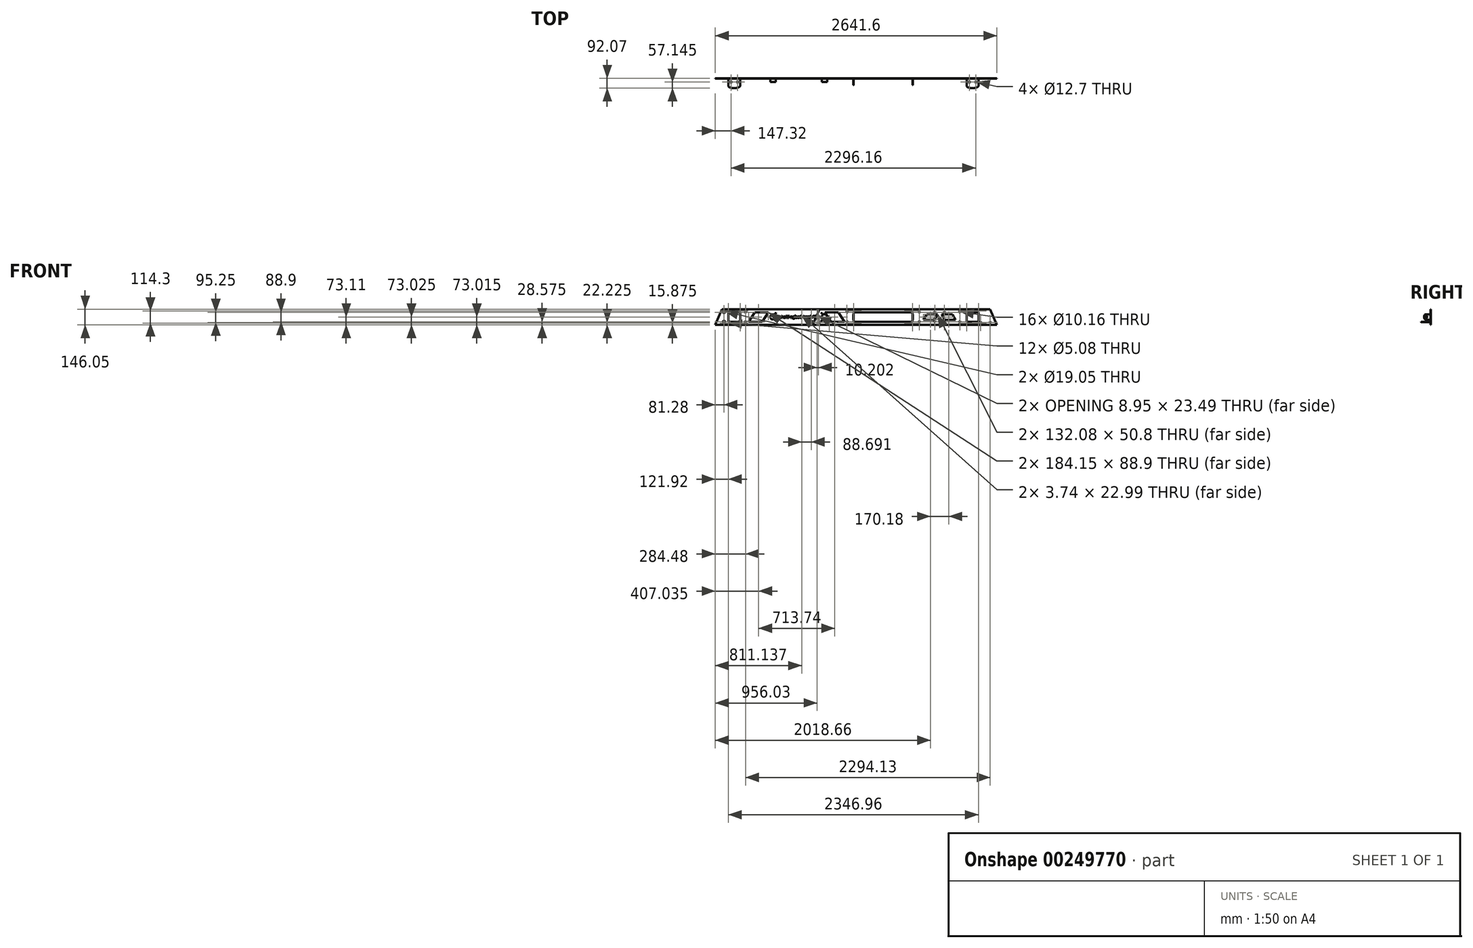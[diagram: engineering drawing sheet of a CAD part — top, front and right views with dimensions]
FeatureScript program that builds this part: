
annotation { "Feature Type Name" : "Feature", "Feature Type Description" : "" }
export const myFeature = defineFeature(function(context is Context, id is Id, definition is map)
    precondition{}
    {
        {
            var Q0;
            Q0=qCreatedBy(makeId("Front.planeOp"),FACE);
            var sketch = newSketch(context, id + "F0", { "sketchPlane" : qUnion([Q0])});
            skLineSegment(sketch, "E0", {"start": v(0, 0) * mm, "end": v(-863.6, 0) * mm});
            skLineSegment(sketch, "E1", {"start": v(-863.6, 0) * mm, "end": v(-800.1, 146.05) * mm});
            skLineSegment(sketch, "E2", {"start": v(-800.1, 146.05) * mm, "end": v(59.06, 146.05) * mm});
            skLineSegment(sketch, "E3", {"start": v(0, 0) * mm, "end": v(0, 425.14) * mm, "construction": true});
            skLineSegment(sketch, "E4.MirrorCS", {"start": v(800.1, 146.05) * mm, "end": v(-59.06, 146.05) * mm});
            skLineSegment(sketch, "E5.MirrorCS", {"start": v(863.6, 0) * mm, "end": v(800.1, 146.05) * mm});
            skLineSegment(sketch, "E6.MirrorCS", {"start": v(0, 0) * mm, "end": v(863.6, 0) * mm});
            skSolve(sketch);
        }
        {
            var Q0;
            Q0=qSketchRegion(id+"F0",true);
            extrude(context, id + "F1", {"entities" : qUnion([Q0]), "oppositeDirection" : true, "depth" : 3.17 * mm});
        }
        {
            var Q0;
            Q0=makeQuery(id+"F1.opExtrude","CAP_FACE",FACE,{"disambiguationData":[OSD([sQuery(id+"F0.wireOp",EDGE,"E0"),sQuery(id+"F0.wireOp",EDGE,"E1"),sQuery(id+"F0.wireOp",EDGE,"E2"),sQuery(id+"F0.wireOp",EDGE,"E4.MirrorCS"),sQuery(id+"F0.wireOp",EDGE,"E5.MirrorCS"),sQuery(id+"F0.wireOp",EDGE,"E6.MirrorCS")])],"isStart":true});
            var sketch = newSketch(context, id + "F2", { "sketchPlane" : qUnion([Q0])});
            skLineSegment(sketch, "E7.0", {"start": v(-863.6, 0) * mm, "end": v(-800.1, 146.05) * mm});
            skLineSegment(sketch, "E8", {"start": v(-800.1, 146.05) * mm, "end": v(-1714.5, 146.05) * mm});
            skLineSegment(sketch, "E9", {"start": v(-1714.5, 146.05) * mm, "end": v(-1778, 0) * mm});
            skLineSegment(sketch, "E10", {"start": v(-1778, 0) * mm, "end": v(-863.6, 0) * mm});
            skSolve(sketch);
        }
        {
            var Q0;
            Q0=qSketchRegion(id+"F2",true);
            var Q1;
            Q1=makeQuery(id+"F1.opExtrude","CAP_FACE",FACE,{"disambiguationData":[OSD([sQuery(id+"F0.wireOp",EDGE,"E0"),sQuery(id+"F0.wireOp",EDGE,"E1"),sQuery(id+"F0.wireOp",EDGE,"E2"),sQuery(id+"F0.wireOp",EDGE,"E4.MirrorCS"),sQuery(id+"F0.wireOp",EDGE,"E5.MirrorCS"),sQuery(id+"F0.wireOp",EDGE,"E6.MirrorCS")])],"isStart":false});
            extrude(context, id + "F3", {"entities" : qUnion([Q0]), "endBound" : BoundingType.UP_TO_SURFACE, "oppositeDirection" : true, "endBoundEntityFace" : qUnion([Q1]), "depth" : 25.4 * mm});
        }
        {
            var Q0;
            Q0=makeQuery(id+"F1.opExtrude","CAP_FACE",FACE,{"disambiguationData":[OSD([sQuery(id+"F0.wireOp",EDGE,"E0"),sQuery(id+"F0.wireOp",EDGE,"E1"),sQuery(id+"F0.wireOp",EDGE,"E2"),sQuery(id+"F0.wireOp",EDGE,"E4.MirrorCS"),sQuery(id+"F0.wireOp",EDGE,"E5.MirrorCS"),sQuery(id+"F0.wireOp",EDGE,"E6.MirrorCS")])],"isStart":false});
            var sketch = newSketch(context, id + "F4", { "sketchPlane" : qUnion([Q0])});
            skLineSegment(sketch, "E11", {"start": v(-831.85, 73.02) * mm, "end": v(1871.27, 73.02) * mm, "construction": true});
            skCircle(sketch, "E12", {"center": v(1236.69, 73.02) * mm, "radius": 25.4 * mm});
            skCircle(sketch, "E13", {"center": v(754.09, 73.02) * mm, "radius": 25.4 * mm});
            skSolve(sketch);
        }
        {
            var Q0;
            Q0=qSketchRegion(id+"F4",true);
            extrude(context, id + "F5", {"entities" : qUnion([Q0]), "operationType" : NewBodyOperationType.ADD, "depth" : 31.75 * mm});
        }
        {
            var Q0;
            Q0=makeQuery(id+"F1.opExtrude","CAP_FACE",FACE,{"disambiguationData":[OSD([sQuery(id+"F0.wireOp",EDGE,"E0"),sQuery(id+"F0.wireOp",EDGE,"E1"),sQuery(id+"F0.wireOp",EDGE,"E2"),sQuery(id+"F0.wireOp",EDGE,"E4.MirrorCS"),sQuery(id+"F0.wireOp",EDGE,"E5.MirrorCS"),sQuery(id+"F0.wireOp",EDGE,"E6.MirrorCS")])],"isStart":true});
            var sketch = newSketch(context, id + "F6", { "sketchPlane" : qUnion([Q0])});
            skLineSegment(sketch, "E14", {"start": v(800.1, 146.05) * mm, "end": v(-1714.5, 146.05) * mm, "construction": true});
            skLineSegment(sketch, "E15", {"start": v(-457.2, 146.05) * mm, "end": v(-457.2, 926.93) * mm, "construction": true});
            skPoint(sketch, "E15.endSnap0", {"position": v(-457.2, 146.05) * mm});
            skLineSegment(sketch, "E16", {"start": v(831.85, 73.02) * mm, "end": v(-1878.84, 73.02) * mm, "construction": true});
            skLineSegment(sketch, "E17.bottom", {"start": v(-478.8, 28.58) * mm, "end": v(72.39, 28.58) * mm});
            skLineSegment(sketch, "E17.top", {"start": v(-478.8, 117.48) * mm, "end": v(72.39, 117.48) * mm});
            skLineSegment(sketch, "E17.left", {"start": v(-478.8, 28.58) * mm, "end": v(-478.8, 117.48) * mm});
            skLineSegment(sketch, "E17.right", {"start": v(72.39, 28.58) * mm, "end": v(72.39, 117.48) * mm});
            skPoint(sketch, "E17.middle", {"position": v(-203.2, 73.02) * mm});
            skLineSegment(sketch, "E18.bottom", {"start": v(690.88, 28.58) * mm, "end": v(579.12, 28.58) * mm});
            skLineSegment(sketch, "E18.top", {"start": v(690.88, 117.48) * mm, "end": v(579.12, 117.47) * mm});
            skLineSegment(sketch, "E18.left", {"start": v(690.88, 28.58) * mm, "end": v(690.88, 117.48) * mm});
            skLineSegment(sketch, "E18.right", {"start": v(579.12, 28.58) * mm, "end": v(579.12, 117.47) * mm});
            skPoint(sketch, "E18.middle", {"position": v(635, 73.03) * mm});
            skCircle(sketch, "E19", {"center": v(135.89, 117.48) * mm, "radius": 5.08 * mm});
            skCircle(sketch, "E20", {"center": v(135.89, 28.58) * mm, "radius": 5.08 * mm});
            skCircle(sketch, "E21", {"center": v(515.62, 28.58) * mm, "radius": 5.08 * mm});
            skCircle(sketch, "E22", {"center": v(515.62, 117.47) * mm, "radius": 5.08 * mm});
            skCircle(sketch, "E23", {"center": v(-542.3, 117.48) * mm, "radius": 5.08 * mm});
            skCircle(sketch, "E24", {"center": v(-542.3, 28.58) * mm, "radius": 5.08 * mm});
            skCircle(sketch, "E25", {"center": v(-478.8, 130.18) * mm, "radius": 2.54 * mm});
            skCircle(sketch, "E26", {"center": v(72.39, 130.18) * mm, "radius": 2.54 * mm});
            skCircle(sketch, "E27.MirrorC", {"center": v(-478.8, 15.87) * mm, "radius": 2.54 * mm});
            skCircle(sketch, "E28.MirrorC", {"center": v(72.39, 15.87) * mm, "radius": 2.54 * mm});
            skCircle(sketch, "E29", {"center": v(579.12, 130.17) * mm, "radius": 2.54 * mm});
            skCircle(sketch, "E30", {"center": v(690.88, 130.18) * mm, "radius": 2.54 * mm});
            skCircle(sketch, "E31.MirrorC", {"center": v(579.12, 15.88) * mm, "radius": 2.54 * mm});
            skCircle(sketch, "E32.MirrorC", {"center": v(690.88, 15.88) * mm, "radius": 2.54 * mm});
            skLineSegment(sketch, "E33.bottom", {"start": v(-1544.32, 28.57) * mm, "end": v(-1656.08, 28.57) * mm});
            skLineSegment(sketch, "E33.top", {"start": v(-1544.32, 117.47) * mm, "end": v(-1656.08, 117.47) * mm});
            skLineSegment(sketch, "E33.left", {"start": v(-1544.32, 28.57) * mm, "end": v(-1544.32, 117.47) * mm});
            skLineSegment(sketch, "E33.right", {"start": v(-1656.08, 28.57) * mm, "end": v(-1656.08, 117.47) * mm});
            skPoint(sketch, "E33.middle", {"position": v(-1600.2, 73.02) * mm});
            skCircle(sketch, "E34", {"center": v(-1493.52, 117.47) * mm, "radius": 5.08 * mm});
            skCircle(sketch, "E35", {"center": v(-1493.52, 28.57) * mm, "radius": 5.08 * mm});
            skCircle(sketch, "E36", {"center": v(-1696.72, 117.47) * mm, "radius": 9.53 * mm});
            skCircle(sketch, "E37", {"center": v(-1696.72, 28.57) * mm, "radius": 9.53 * mm});
            skCircle(sketch, "E38", {"center": v(-1656.08, 130.17) * mm, "radius": 2.54 * mm});
            skCircle(sketch, "E39", {"center": v(-1544.32, 130.17) * mm, "radius": 2.54 * mm});
            skCircle(sketch, "E40.MirrorC", {"center": v(-1656.08, 15.87) * mm, "radius": 2.54 * mm});
            skCircle(sketch, "E41.MirrorC", {"center": v(-1544.32, 15.87) * mm, "radius": 2.54 * mm});
            skLineSegment(sketch, "E42", {"start": v(135.89, 117.47) * mm, "end": v(515.62, 117.48) * mm, "construction": true});
            skLineSegment(sketch, "E43", {"start": v(325.75, 117.48) * mm, "end": v(325.75, 228.13) * mm, "construction": true});
            skCircle(sketch, "E44", {"center": v(371.1, 117.48) * mm, "radius": 5.08 * mm});
            skCircle(sketch, "E45.MirrorC", {"center": v(280.42, 117.48) * mm, "radius": 5.08 * mm});
            skCircle(sketch, "E46.MirrorC", {"center": v(280.42, 28.57) * mm, "radius": 5.08 * mm});
            skCircle(sketch, "E47.MirrorC", {"center": v(371.1, 28.57) * mm, "radius": 5.08 * mm});
            skLineSegment(sketch, "E48", {"start": v(344.8, 98.42) * mm, "end": v(446.4, 98.42) * mm});
            skLineSegment(sketch, "E49", {"start": v(446.4, 98.43) * mm, "end": v(476.88, 47.62) * mm});
            skLineSegment(sketch, "E50", {"start": v(476.88, 47.62) * mm, "end": v(375.28, 47.62) * mm});
            skLineSegment(sketch, "E51", {"start": v(375.28, 47.62) * mm, "end": v(344.8, 98.42) * mm});
            skLineSegment(sketch, "E52.MirrorCS", {"start": v(306.7, 98.42) * mm, "end": v(205.1, 98.42) * mm});
            skLineSegment(sketch, "E53.MirrorCS", {"start": v(276.22, 47.62) * mm, "end": v(306.7, 98.42) * mm});
            skLineSegment(sketch, "E54.MirrorCS", {"start": v(174.62, 47.62) * mm, "end": v(276.22, 47.62) * mm});
            skLineSegment(sketch, "E55.MirrorCS", {"start": v(205.1, 98.43) * mm, "end": v(174.62, 47.62) * mm});
            skLineSegment(sketch, "E56", {"start": v(-1278.9, 117.47) * mm, "end": v(-1405.9, 117.47) * mm});
            skLineSegment(sketch, "E57", {"start": v(-1405.9, 117.47) * mm, "end": v(-1463.04, 28.57) * mm});
            skLineSegment(sketch, "E58", {"start": v(-1463.04, 28.57) * mm, "end": v(-1336.04, 28.57) * mm});
            skLineSegment(sketch, "E59", {"start": v(-1336.04, 28.57) * mm, "end": v(-1278.9, 117.47) * mm});
            skCircle(sketch, "E60", {"center": v(-779.49, 107.95) * mm, "radius": 3.18 * mm});
            skCircle(sketch, "E61", {"center": v(-1211.29, 107.95) * mm, "radius": 3.17 * mm});
            skCircle(sketch, "E62.MirrorC", {"center": v(-1211.29, 38.1) * mm, "radius": 3.17 * mm});
            skCircle(sketch, "E63.MirrorC", {"center": v(-779.49, 38.1) * mm, "radius": 3.18 * mm});
            skLineSegment(sketch, "E64", {"start": v(-622.3, 117.48) * mm, "end": v(-749.3, 117.48) * mm});
            skLineSegment(sketch, "E65", {"start": v(-749.3, 117.48) * mm, "end": v(-692.15, 28.58) * mm});
            skLineSegment(sketch, "E66", {"start": v(-692.15, 28.58) * mm, "end": v(-565.15, 28.58) * mm});
            skLineSegment(sketch, "E67", {"start": v(-565.15, 28.58) * mm, "end": v(-622.3, 117.48) * mm});
            skSolve(sketch);
        }
        {
            var Q0;
            Q0=qSketchRegion(id+"F6",true);
            extrude(context, id + "F7", {"entities" : qUnion([Q0]), "operationType" : NewBodyOperationType.REMOVE, "oppositeDirection" : true, "depth" : 25.4 * mm});
        }
        {
            var Q0;
            Q0=makeQuery(id+"F1.opExtrude","CAP_FACE",FACE,{"disambiguationData":[OSD([sQuery(id+"F0.wireOp",EDGE,"E0"),sQuery(id+"F0.wireOp",EDGE,"E1"),sQuery(id+"F0.wireOp",EDGE,"E2"),sQuery(id+"F0.wireOp",EDGE,"E4.MirrorCS"),sQuery(id+"F0.wireOp",EDGE,"E5.MirrorCS"),sQuery(id+"F0.wireOp",EDGE,"E6.MirrorCS")])],"isStart":true});
            var sketch = newSketch(context, id + "F8", { "sketchPlane" : qUnion([Q0])});
            skCircle(sketch, "E68", {"center": v(800.6, 22.23) * mm, "radius": 5.08 * mm});
            skCircle(sketch, "E69", {"center": v(709.93, 22.23) * mm, "radius": 5.08 * mm});
            skLineSegment(sketch, "E70", {"start": v(0, 0) * mm, "end": v(0, -220.42) * mm, "construction": true});
            skCircle(sketch, "E71.MirrorC", {"center": v(-709.93, 22.22) * mm, "radius": 5.08 * mm});
            skCircle(sketch, "E72.MirrorC", {"center": v(-800.6, 22.22) * mm, "radius": 5.08 * mm});
            skSolve(sketch);
        }
        {
            var Q0;
            Q0=qSketchRegion(id+"F8",true);
            var Q1;
            Q1=makeQuery(id+"F1.opExtrude","CAP_FACE",FACE,{"disambiguationData":[OSD([sQuery(id+"F0.wireOp",EDGE,"E0"),sQuery(id+"F0.wireOp",EDGE,"E1"),sQuery(id+"F0.wireOp",EDGE,"E2"),sQuery(id+"F0.wireOp",EDGE,"E4.MirrorCS"),sQuery(id+"F0.wireOp",EDGE,"E5.MirrorCS"),sQuery(id+"F0.wireOp",EDGE,"E6.MirrorCS")])],"isStart":false});
            extrude(context, id + "F9", {"entities" : qUnion([Q0]), "operationType" : NewBodyOperationType.REMOVE, "endBound" : BoundingType.UP_TO_SURFACE, "oppositeDirection" : true, "endBoundEntityFace" : qUnion([Q1]), "depth" : 25.4 * mm});
        }
        {
            var Q0;
            Q0=makeQuery(id+"F7.boolean.opBoolean","COPY",FACE,{"derivedFrom":makeQuery(id+"F7.opExtrude","SWEPT_FACE",FACE,{"disambiguationData":[OSD([sQuery(id+"F6.wireOp",EDGE,"E33.bottom")])]})});
            var sketch = newSketch(context, id + "F10", { "sketchPlane" : qUnion([Q0])});
            skLineSegment(sketch, "E73", {"start": v(-1600.2, 3.18) * mm, "end": v(-1600.2, 59.04) * mm, "construction": true});
            skPoint(sketch, "E73.endSnap0", {"position": v(-1600.2, 3.18) * mm});
            skLineSegment(sketch, "E74", {"start": v(-1656.08, 3.18) * mm, "end": v(-1656.08, 71.76) * mm});
            skLineSegment(sketch, "E75.MirrorCS", {"start": v(-1544.32, 3.18) * mm, "end": v(-1544.32, 71.76) * mm});
            skEllipticalArc(sketch, "E76", {});
            skLineSegment(sketch, "E77", {"start": v(-1656.08, 3.18) * mm, "end": v(-1544.32, 3.18) * mm});
            skCircle(sketch, "E78", {"center": v(-1630.68, 34.93) * mm, "radius": 6.35 * mm});
            skCircle(sketch, "E79.MirrorC", {"center": v(-1569.72, 34.93) * mm, "radius": 6.35 * mm});
            skLineSegment(sketch, "E80", {"start": v(690.88, 3.18) * mm, "end": v(579.12, 3.17) * mm, "construction": true});
            skLineSegment(sketch, "E81", {"start": v(635, 3.18) * mm, "end": v(635, 23.98) * mm, "construction": true});
            skLineSegment(sketch, "E82", {"start": v(579.12, 3.17) * mm, "end": v(579.12, 71.76) * mm});
            skLineSegment(sketch, "E83.MirrorCS", {"start": v(690.88, 3.17) * mm, "end": v(690.88, 71.76) * mm});
            skEllipticalArc(sketch, "E84", {});
            skLineSegment(sketch, "E85", {"start": v(579.12, 3.17) * mm, "end": v(690.88, 3.18) * mm});
            skCircle(sketch, "E86", {"center": v(604.52, 34.93) * mm, "radius": 6.35 * mm});
            skCircle(sketch, "E87.MirrorC", {"center": v(665.48, 34.93) * mm, "radius": 6.35 * mm});
            const initialGuessF10  = {"E76": [-1.6002, 0.071755, -1, 0, 0.05588, 0.02032, 3.141592653589793, 0], "E84": [0.635, 0.071755, -1, 0, 0.05588, 0.02032, 3.141592653589793, 0]};
            skSetInitialGuess(sketch, initialGuessF10);
            skSolve(sketch);
        }
        {
            var Q0;
            Q0=qSketchRegion(id+"F10",true);
            extrude(context, id + "F11", {"entities" : qUnion([Q0]), "operationType" : NewBodyOperationType.ADD, "oppositeDirection" : true, "depth" : 3.17 * mm});
        }
        {
            var Q0;
            Q0=makeQuery(id+"F7.boolean.opBoolean","COPY",FACE,{"derivedFrom":makeQuery(id+"F7.opExtrude","SWEPT_FACE",FACE,{"disambiguationData":[OSD([sQuery(id+"F6.wireOp",EDGE,"E17.right")])]})});
            var sketch = newSketch(context, id + "F12", { "sketchPlane" : qUnion([Q0])});
            skLineSegment(sketch, "E88", {"start": v(-3.18, 73.02) * mm, "end": v(-34, 73.02) * mm, "construction": true});
            skLineSegment(sketch, "E89", {"start": v(-3.18, 98.42) * mm, "end": v(-47.62, 98.42) * mm});
            skLineSegment(sketch, "E90.MirrorCS", {"start": v(-3.18, 47.62) * mm, "end": v(-47.62, 47.62) * mm});
            skEllipticalArc(sketch, "E91", {});
            skCircle(sketch, "E92", {"center": v(-40, 73.02) * mm, "radius": 6.35 * mm});
            skLineSegment(sketch, "E93", {"start": v(-3.18, 98.42) * mm, "end": v(-3.18, 47.62) * mm});
            const initialGuessF12  = {"E91": [-0.047625, 0.073025, 0, 1, 0.0254, 0.01524, 0, 3.141592653589793]};
            skSetInitialGuess(sketch, initialGuessF12);
            skSolve(sketch);
        }
        {
            var Q0;
            Q0=qSketchRegion(id+"F12",true);
            extrude(context, id + "F13", {"entities" : qUnion([Q0]), "oppositeDirection" : true, "depth" : 3.17 * mm});
        }
        {
            var Q0;
            Q0=makeQuery(id+"F7.boolean.opBoolean","COPY",FACE,{"derivedFrom":makeQuery(id+"F7.opExtrude","SWEPT_FACE",FACE,{"disambiguationData":[OSD([sQuery(id+"F6.wireOp",EDGE,"E17.right")])]})});
            var Q1;
            Q1=makeQuery(id+"F7.boolean.opBoolean","COPY",FACE,{"derivedFrom":makeQuery(id+"F7.opExtrude","SWEPT_FACE",FACE,{"disambiguationData":[OSD([sQuery(id+"F6.wireOp",EDGE,"E17.left")])]})});
            cPlane(context, id + "F14", {"entities" : qUnion([Q0, Q1]), "cplaneType" : CPlaneType.MID_PLANE, "offset" : 25.4 * mm, "width" : 152.4 * mm, "height" : 152.4 * mm});
        }
        {
            var Q0;
            Q0=makeQuery(id+"F13.opExtrude","SWEPT_BODY",BODY,{"disambiguationData":[OSD([sQuery(id+"F12.wireOp",EDGE,"E89"),sQuery(id+"F12.wireOp",EDGE,"E90.MirrorCS"),sQuery(id+"F12.wireOp",EDGE,"E91"),sQuery(id+"F12.wireOp",EDGE,"E92"),sQuery(id+"F12.wireOp",EDGE,"E93")])]});
            var Q1;
            Q1=qCreatedBy(id+"F14.planeOp",FACE);
            mirror(context, id + "F15", {"operationType" : NewBodyOperationType.ADD, "entities" : qUnion([Q0]), "mirrorPlane" : qUnion([Q1])});
        }
        {
            var Q0;
            Q0=makeQuery(id+"F1.opExtrude","SWEPT_BODY",BODY,{"disambiguationData":[OSD([sQuery(id+"F0.wireOp",EDGE,"E0"),sQuery(id+"F0.wireOp",EDGE,"E1"),sQuery(id+"F0.wireOp",EDGE,"E2"),sQuery(id+"F0.wireOp",EDGE,"E4.MirrorCS"),sQuery(id+"F0.wireOp",EDGE,"E5.MirrorCS"),sQuery(id+"F0.wireOp",EDGE,"E6.MirrorCS")])]});
            var Q1;
            Q1=makeQuery(id+"F3.opExtrude","SWEPT_BODY",BODY,{"disambiguationData":[OSD([sQuery(id+"F2.wireOp",EDGE,"E7.0"),sQuery(id+"F2.wireOp",EDGE,"E8"),sQuery(id+"F2.wireOp",EDGE,"E9"),sQuery(id+"F2.wireOp",EDGE,"E10")])]});
            var Q2;
            Q2=qCreatedBy(makeId("Front.planeOp"),FACE);
            mirror(context, id + "F16", {"entities" : qUnion([Q0, Q1]), "mirrorPlane" : qUnion([Q2])});
        }
        {
            var Q0;
            Q0=makeQuery(id+"F1.opExtrude","SWEPT_BODY",BODY,{"disambiguationData":[OSD([sQuery(id+"F0.wireOp",EDGE,"E0"),sQuery(id+"F0.wireOp",EDGE,"E1"),sQuery(id+"F0.wireOp",EDGE,"E2"),sQuery(id+"F0.wireOp",EDGE,"E4.MirrorCS"),sQuery(id+"F0.wireOp",EDGE,"E5.MirrorCS"),sQuery(id+"F0.wireOp",EDGE,"E6.MirrorCS")])]});
            var Q1;
            Q1=makeQuery(id+"F3.opExtrude","SWEPT_BODY",BODY,{"disambiguationData":[OSD([sQuery(id+"F2.wireOp",EDGE,"E7.0"),sQuery(id+"F2.wireOp",EDGE,"E8"),sQuery(id+"F2.wireOp",EDGE,"E9"),sQuery(id+"F2.wireOp",EDGE,"E10")])]});
            deleteBodies(context, id + "F17", {"entities" : qUnion([Q0, Q1])});
        }
        {
            var Q0;
            Q0=makeQuery(id+"F16.opPattern","COPY",FACE,{"derivedFrom":makeQuery(id+"F3.opExtrude","CAP_FACE",FACE,{"disambiguationData":[OSD([sQuery(id+"F2.wireOp",EDGE,"E7.0"),sQuery(id+"F2.wireOp",EDGE,"E8"),sQuery(id+"F2.wireOp",EDGE,"E9"),sQuery(id+"F2.wireOp",EDGE,"E10")])],"isStart":true}),"instanceName":"1"});
            var sketch = newSketch(context, id + "F18", { "sketchPlane" : qUnion([Q0])});
            skText(sketch, "E94", { "text": "Off-Road Design Works", "fontName": "AllertaStencil-Regular.ttf"});
            skLineSegment(sketch, "E95", {"start": v(804.89, 73.02) * mm, "end": v(778.37, 73.02) * mm, "construction": true});
            const initialGuessF18  = {"E94": [0.80489, 0.06152, 1, 0, 0.023]};
            skSetInitialGuess(sketch, initialGuessF18);
            skSolve(sketch);
        }
        {
            var Q0;
            Q0 = qSketchRegion(id + "F18", true);
            var Q1;
            Q1=makeQuery(id+"F16.opPattern","COPY",FACE,{"derivedFrom":makeQuery(id+"F3.opExtrude","CAP_FACE",FACE,{"disambiguationData":[OSD([sQuery(id+"F2.wireOp",EDGE,"E7.0"),sQuery(id+"F2.wireOp",EDGE,"E8"),sQuery(id+"F2.wireOp",EDGE,"E9"),sQuery(id+"F2.wireOp",EDGE,"E10")])],"isStart":false}),"instanceName":"1"});
            extrude(context, id + "F19", {"entities" : qUnion([Q0]), "operationType" : NewBodyOperationType.REMOVE, "endBound" : BoundingType.UP_TO_SURFACE, "oppositeDirection" : true, "endBoundEntityFace" : qUnion([Q1]), "depth" : 25.4 * mm});
        }
    });
